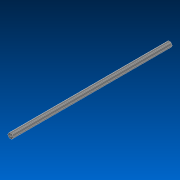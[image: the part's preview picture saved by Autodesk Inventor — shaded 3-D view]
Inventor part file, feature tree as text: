
AUTODESK INVENTOR PART (.ipt)
format: ipt  version: 2022.2 (Build 262287000, 287)  size: 121,344 bytes
history: native  units: in
note: dims shown in document units (in); Inventor stores cm internally (conversion verified against a paired STEP export)
features: extrude x1, sketch x1, other x1
ambient origin geometry x8: Origin, YZ Plane, XZ Plane, XY Plane, X Axis, Y Axis, Z Axis, Center Point
bodies: Solid1 (feature_tree)
feature tree (3):
  extrude  "Extrusion1"  TaperAngle=0.0deg  [1 undecoded]
  sketch  "Sketch1"  dims[d0=19.0in d1=0.0in]
  other  "Cut-Extrude2"
note: 1 required parameter value undecoded (feature->parameter linkage not recoverable at this tier; creation-order binding heuristic only, values carry confidence <= 0.55)
